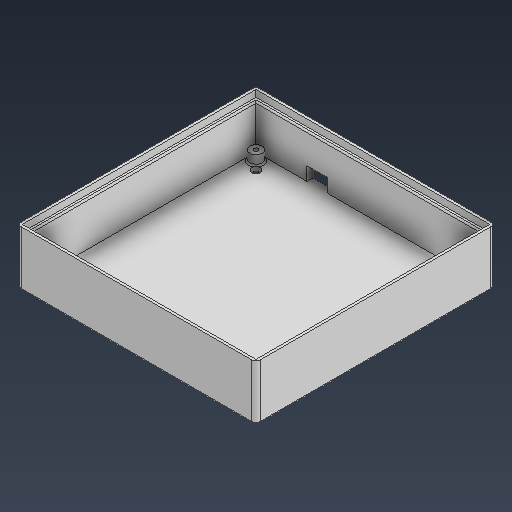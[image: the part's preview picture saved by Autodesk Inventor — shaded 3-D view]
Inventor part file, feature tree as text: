
AUTODESK INVENTOR PART (.ipt)
format: ipt  version: 2025.3 (Build 293356000, 356)  size: 274,944 bytes
history: native  units: mm
features: sketch x9, extrude x7, projected_geometry x5, fillet x4, hole x1
ambient origin geometry x8: Origin, YZ Plane, XZ Plane, XY Plane, X Axis, Y Axis, Z Axis, Center Point
bodies: Solid1 (feature_tree)
feature tree (26):
  extrude  "Extrusion1"  Depth=175.0mm
  extrude  "Extrusion2"  Depth=37.09mm TaperAngle=0.0deg
  extrude  "Extrusion3"  Depth=171.2mm
  extrude  "Extrusion5"  Depth=165.0mm
  hole  "Hole1"  [1 undecoded]
  extrude  "Extrusion7"  Depth=27.0mm
  extrude  "Extrusion8"  Depth=5.0mm
  extrude  "Extrusion9"  Depth=5.0mm
  fillet  "Fillet1"  Radius=7.0mm
  fillet  "Fillet2"  Radius=9.2mm
  fillet  "Fillet3"  Radius=9.2mm
  fillet  "Fillet4"  Radius=9.2mm
  sketch  "Sketch1"  dims[d0=175.0mm d1=175.0mm]
  sketch  "Sketch2"  dims[d8=5.0mm d9=0.0mm d20=171.2mm]
  projected_geometry  "Projected Loop1"
  sketch  "Sketch3"  dims[d21=166.0mm d22=165.0mm]
  projected_geometry  "Projected Loop2"
  sketch  "Sketch5"  dims[d23=5.0mm d27=5.0mm]
  projected_geometry  "Projected Loop4"
  sketch  "Sketch8"  dims[d34=8.0mm d35=27.0mm]
  sketch  "Sketch9"  dims[d36=5.0mm d37=5.0mm]
  projected_geometry  "Projected Loop5"
  sketch  "Sketch10"  dims[d38=5.0mm d39=5.0mm d40=7.0mm d41=0.0mm d45=9.2mm d46=9.2mm d47=9.2mm]
  sketch  "Sketch Rectangular Pattern1"  dims[d2=3.0mm d3=0.0mm d5=37.09mm d6=0.0mm]
  sketch  "Sketch11"  dims[d48=9.2mm d51=3.2mm d52=6.0mm d53=4.0mm d54=2.0mm d55=90.0deg d56=8.0mm d57=20.594885mm d58=44.765mm d59=15.0mm d60=10.0mm d61=1.6mm d62=10.0mm d63=0.0mm d64=6.4mm d65=16.0mm d66=16.0mm d67=20.0mm d69=143.0mm d70=20.0mm d72=143.0mm d75=10.0mm d76=0.0mm d77=6.0mm d78=6.0mm d79=6.0mm d80=6.0mm d81=4.0mm d82=0.0mm d83=3.0mm d84=1.0mm d85=1.1mm d86=1.0mm]
  projected_geometry  "Projected Loop6"
note: 1 required parameter value undecoded (feature->parameter linkage not recoverable at this tier; creation-order binding heuristic only, values carry confidence <= 0.55)
